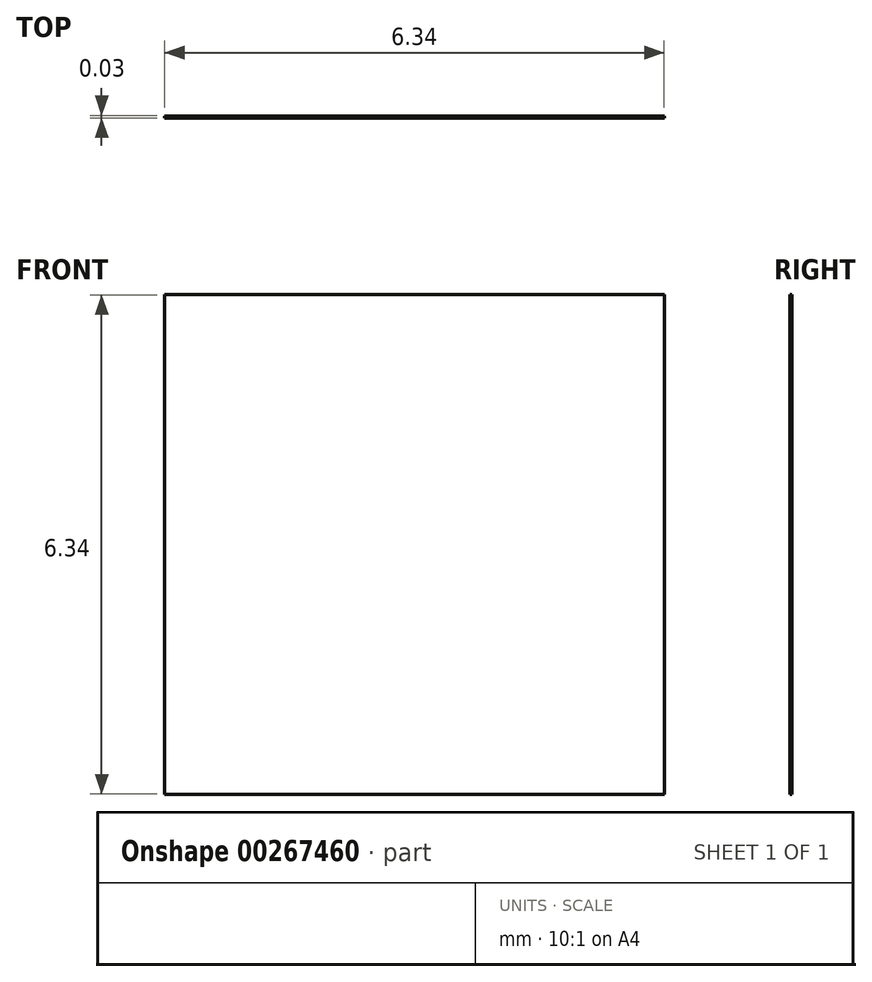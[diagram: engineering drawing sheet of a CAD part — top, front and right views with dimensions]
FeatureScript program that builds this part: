
annotation { "Feature Type Name" : "Feature", "Feature Type Description" : "" }
export const myFeature = defineFeature(function(context is Context, id is Id, definition is map)
    precondition{}
    {
        {
            var Q0;
            Q0=qCreatedBy(makeId("Front.planeOp"),FACE);
            var sketch = newSketch(context, id + "F0", { "sketchPlane" : qUnion([Q0])});
            skLineSegment(sketch, "E0.bottom", {"start": v(-3.18, 3.18) * mm, "end": v(3.18, 3.18) * mm});
            skLineSegment(sketch, "E0.top", {"start": v(-3.18, -3.18) * mm, "end": v(3.18, -3.18) * mm});
            skLineSegment(sketch, "E0.left", {"start": v(-3.18, 3.18) * mm, "end": v(-3.18, -3.18) * mm});
            skLineSegment(sketch, "E0.right", {"start": v(3.18, 3.18) * mm, "end": v(3.18, -3.18) * mm});
            skPoint(sketch, "E0.middle", {"position": v(0, 0) * mm});
            skSolve(sketch);
        }
        {
            var Q0;
            Q0 = qSketchRegion(id + "F0", true);
            extrude(context, id + "F1", {"entities" : qUnion([Q0]), "oppositeDirection" : true, "depth" : 0.03 * mm});
        }
    });
